# Revit family: Tub-Single Bowl with Cabinet-Clark Utility 42L1
name_source: partatom
category: Plumbing Fixtures
revit_build: Autodesk Revit Architecture 2012 (Build: 20110916_2132(x64)
units: mm (PartAtom-declared; Revit-internal decimal feet)

## types (1)
- Utility 42L
    Assembly Code = D2010420
    CW Connection = No
    Cabinet = Metal-Steel-Powdercoated-Caroma White
    Cost = 0 $
    Default Elevation = 0 mm  [stored 0 ft]
    Description = Utility 42 Litre Laundry Tub & Cabinet
    HW Connection = No
    Height_ANZRS = 870 mm
    Keynote = SK
    Length_ANZRS = 600 mm
    Manufacturer = Clark
    Material_ANZRS = Metal-Stainless-Caroma
    Model = F6111
    Type Comments = Includes basket waste, Bowl Volume 42L, Carton size 615 x 510 x 910, Carton weight 13.5kg, Match with Dorf Eclipse mixer range, Includes side entry suitable for concealed taps
    URL = http://www.clark.com.au
    Vent Connection = No
    WFU = 2
    Waste Connection = Yes
    Waste Radius = 30 mm  [stored 0.0984252 ft]
    Width_ANZRS = 527 mm  [stored 1.729 ft]

note: [stored X ft] marks values corroborated as IEEE doubles in the binary element streams (Revit-internal decimal feet)

## geometry (parser evidence)
native form markers: Blend x2, Sweep x2
no freeform markers — native parametric forms only
